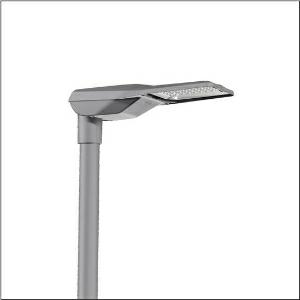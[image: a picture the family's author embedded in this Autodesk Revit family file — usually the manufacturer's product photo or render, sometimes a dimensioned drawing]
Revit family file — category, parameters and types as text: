
# Revit family: streetlight_sl_21_iq_mini___st0_5a_5xe2b31d08hb_2e1a
name_source: partatom
category: Lighting Fixtures
units: mm (PartAtom-declared; Revit-internal decimal feet)

## family parameters
Cut with Voids When Loaded = No
Host = Face
Light Source = No
Part Type = Normal
Room Calculation Point = No
Round Connector Dimension = Use Diameter
Shared = No

## types (1)
- --- (1 x LED, 9450 lm, 70.9 W, 3000K)
    Apparent Load = 71 VA
    CIE Flux Codes = 41 75 97 100 100
    Color Rendering = 70
    Color Temperature = 3000K
    Default Elevation = 1800 mm
    Description = Streetlight SL 21 mini, mast luminaire, primary light control with lens, of PMMA, primary optical cover: cover, of toughened safety glass, transparent, light distribution: ST0.5a, light emission: direct distribution, primary light characteristic: asymmetric, installation type: post-top, side-entry, LED, High Power LED, rated luminous flux: 9.450lm, luminous efficacy: 133lm/W, light colour: 730, colour temperature: 3000K, control gear: ECG iQ, control: Auto-Match, Temp-Guard, Lumen-Switch, Night-Set, Smart-Wire, Light-Fading, Desk-Remote (wireless, voltage-free reading and setting of iQ features in the workshop via application-optimized NFC function/RFID function), optimised constant luminous flux control (CLO 2.0), mains connection: 220..240V, AC, 50/60Hz, start of lifetime: 71W, end of lifetime: 75W, reduction: 31W, luminaire housing, of diecast aluminium, powder-coated, Siteco® metallic grey (DB 702S), corrosivity category C5 according to DIN EN ISO 12944, length: 628mm, width: 235mm, height: 110mm, spigot size: 60/76mm (post-top) and 42/60/76mm (side-entry), mast flange for spigot size: 42mm: 5XC10008XM4, 60mm: 5XC10008XM2, 76/60mm: 5XC10108XM1, protection rating (complete): IP66, insulation class (complete): insulation class II (safety insulation), certification: CE, ENEC, VDE, impact resistance: IK09, permissible operating ambient temperature for outdoor applications: -40..+50°C, standard-compliant lighting for roads and squares, packaging unit: 1 piece

Light Distribution: ST0.5a
    Height = 110 mm
    Lamp = 1 x LED
    Lamp Light Flux = 9450 lm
    Lamp Power = 70.9 W
    Lamp count = 1
    Length = 625 mm
    Luminous efficacy = 133 lm/W
    Manufacturer = Siteco
    ModVariant = No
    Model = 5XE2B31D08HB
    Number of Poles = 1
    OnlyDefault = Yes
    Power Factor = 1
    Product Name = Streetlight SL 21 iQ mini | ST0.5a
    Product group = mast luminaire | pylon top
    ProductGroupID = 6100
    Protection Class = Protection class II
    Protection Degree = IP 66
    RLX_Detail_Level = 1
    RlxData = <blob elided: 103365 chars, md5=844547e1>
    Socket = socket
    Standby Power = 0 W
    System Light Flux = 9450 lm
    System Power = 71 W
    Type Comments = factory setting: luminous flux: 100 % | dim-lin: 254 | 711 mA
    Type Image = l_1003519.jpg
    URL = http://relux.com
    VarID = @adj_069873
    Voltage = 0 V
    Weight = 0.00 kg
    Width = 234 mm

## geometry (parser evidence)
native form markers: Blend x4, Sweep x10
no freeform markers — native parametric forms only
